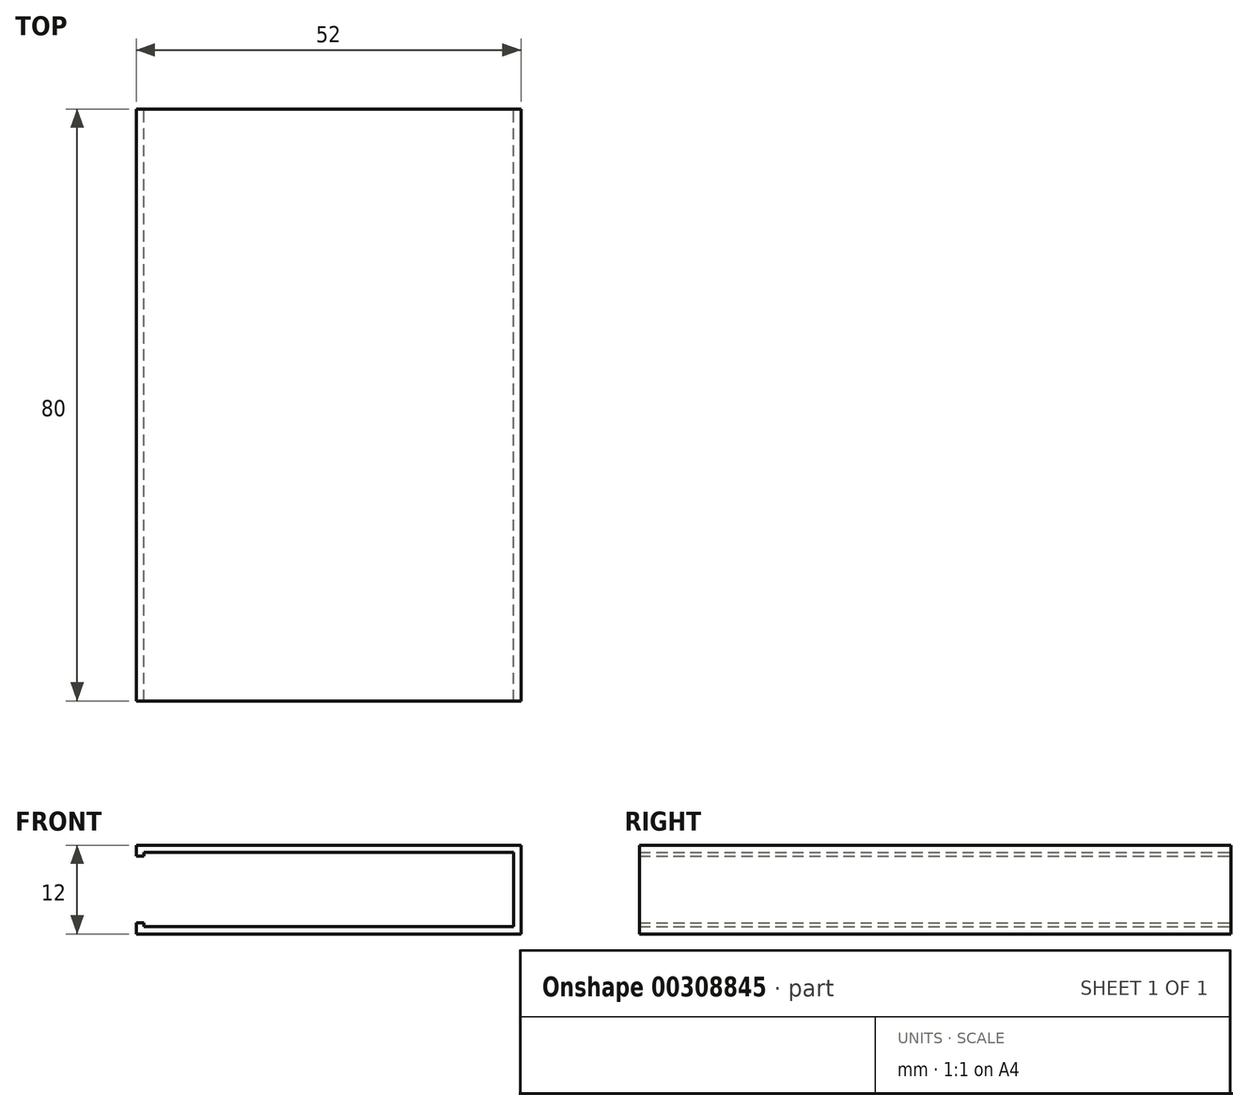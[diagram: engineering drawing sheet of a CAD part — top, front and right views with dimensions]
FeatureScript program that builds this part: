
annotation { "Feature Type Name" : "Feature", "Feature Type Description" : "" }
export const myFeature = defineFeature(function(context is Context, id is Id, definition is map)
    precondition{}
    {
        {
            var Q0;
            Q0=qCreatedBy(makeId("Front.planeOp"),FACE);
            var sketch = newSketch(context, id + "F0", { "sketchPlane" : qUnion([Q0])});
            skLineSegment(sketch, "E0", {"start": v(-25.03, 5.75) * mm, "end": v(26.97, 5.75) * mm});
            skLineSegment(sketch, "E1", {"start": v(26.97, 5.75) * mm, "end": v(26.97, -6.25) * mm});
            skLineSegment(sketch, "E2", {"start": v(26.97, -6.25) * mm, "end": v(-25.03, -6.25) * mm});
            skLineSegment(sketch, "E3.0", {"start": v(-24.03, 4.75) * mm, "end": v(25.97, 4.75) * mm});
            skLineSegment(sketch, "E4.0", {"start": v(25.97, 4.75) * mm, "end": v(25.97, -5.25) * mm});
            skLineSegment(sketch, "E5.0", {"start": v(25.97, -5.25) * mm, "end": v(-24.03, -5.25) * mm});
            skLineSegment(sketch, "E6", {"start": v(-25.03, 5.75) * mm, "end": v(-25.03, 4.25) * mm});
            skLineSegment(sketch, "E7", {"start": v(-25.03, -6.25) * mm, "end": v(-25.03, -4.75) * mm});
            skLineSegment(sketch, "E8", {"start": v(-25.03, -4.75) * mm, "end": v(-24.03, -4.75) * mm});
            skLineSegment(sketch, "E9", {"start": v(-24.03, -4.75) * mm, "end": v(-24.03, -5.25) * mm});
            skLineSegment(sketch, "E10", {"start": v(-25.03, 4.25) * mm, "end": v(-24.03, 4.25) * mm});
            skLineSegment(sketch, "E11", {"start": v(-24.03, 4.25) * mm, "end": v(-24.03, 4.75) * mm});
            skSolve(sketch);
        }
        {
            var Q0;
            Q0=makeQuery(id+"F0.imprint","IMPRINT",FACE,{"disambiguationData":[TD([[makeQuery(id+"F0.imprint","IMPRINT",EDGE,{"derivedFrom":sQuery(id+"F0.wireOp",EDGE,"E0")}),-1.0]])]});
            extrude(context, id + "F1", {"entities" : qUnion([Q0]), "depth" : 80 * mm});
        }
    });
